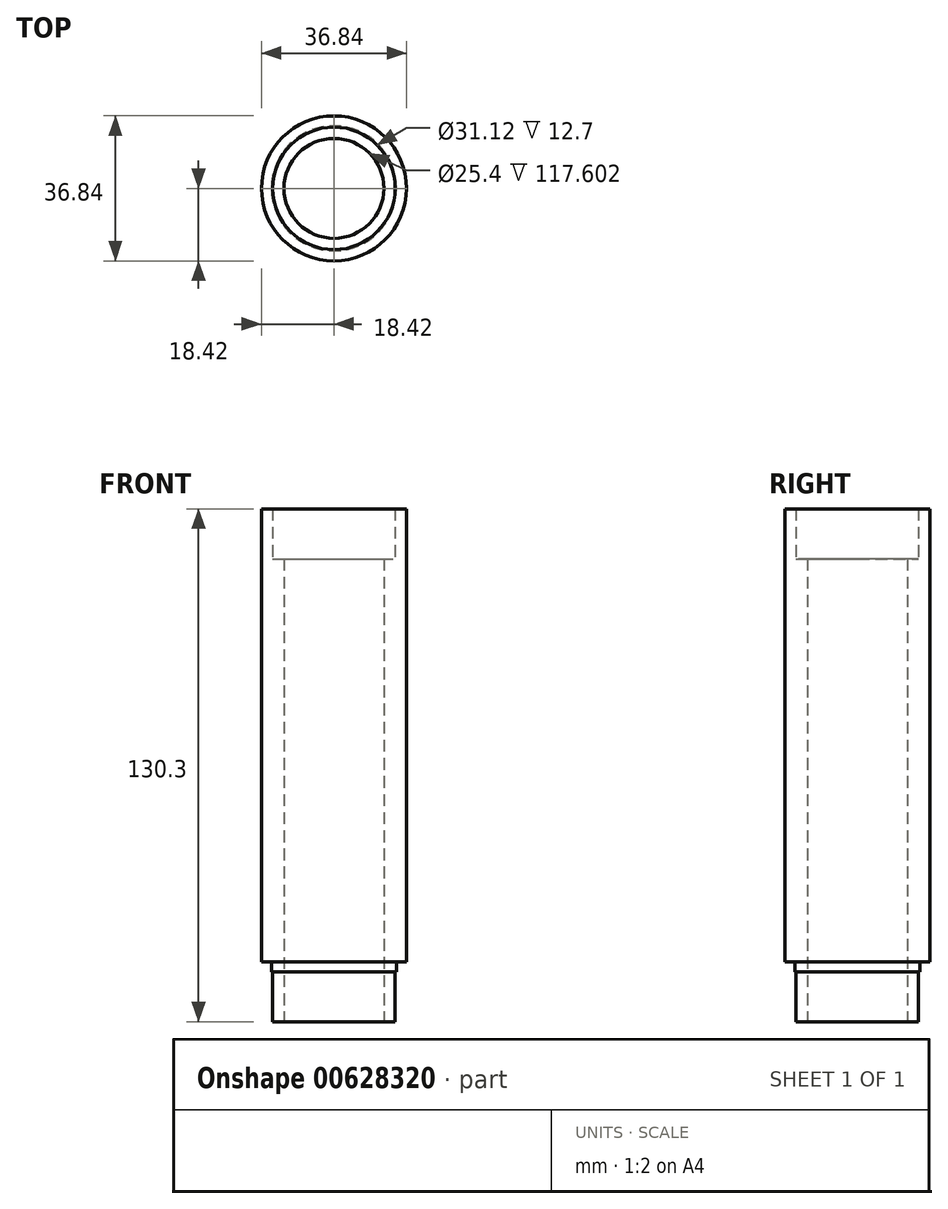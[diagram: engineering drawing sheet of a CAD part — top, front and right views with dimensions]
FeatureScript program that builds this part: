
annotation { "Feature Type Name" : "Feature", "Feature Type Description" : "" }
export const myFeature = defineFeature(function(context is Context, id is Id, definition is map)
    precondition{}
    {
        {
            var Q0;
            Q0=qCreatedBy(makeId("Front.planeOp"),FACE);
            var sketch = newSketch(context, id + "F0", { "sketchPlane" : qUnion([Q0])});
            skLineSegment(sketch, "E0.trimOffspring", {"start": v(18.41, 70.5) * mm, "end": v(18.42, -42.94) * mm});
            skLineSegment(sketch, "E1", {"start": v(18.42, -42.94) * mm, "end": v(15.87, -42.94) * mm});
            skLineSegment(sketch, "E2", {"start": v(15.87, -42.94) * mm, "end": v(15.87, -45.48) * mm});
            skLineSegment(sketch, "E3", {"start": v(12.7, 59.42) * mm, "end": v(12.7, -58.18) * mm});
            skLineSegment(sketch, "E4", {"start": v(12.7, -58.18) * mm, "end": v(15.56, -58.18) * mm});
            skLineSegment(sketch, "E5", {"start": v(15.56, -58.18) * mm, "end": v(15.56, -45.48) * mm});
            skLineSegment(sketch, "E6", {"start": v(15.56, -45.48) * mm, "end": v(15.87, -45.48) * mm});
            skLineSegment(sketch, "E7", {"start": v(15.56, 72.12) * mm, "end": v(15.56, 59.42) * mm});
            skLineSegment(sketch, "E8", {"start": v(15.56, 72.12) * mm, "end": v(18.41, 72.12) * mm});
            skLineSegment(sketch, "E9", {"start": v(18.41, 72.12) * mm, "end": v(18.41, 70.5) * mm});
            skLineSegment(sketch, "E10", {"start": v(15.56, 59.42) * mm, "end": v(12.7, 59.42) * mm});
            skLineSegment(sketch, "E11", {"start": v(0, 0) * mm, "end": v(0, 42.91) * mm});
            skSolve(sketch);
        }
        {
            var Q0;
            Q0=makeQuery(id+"F0.imprint","IMPRINT",FACE,{"disambiguationData":[TD([[makeQuery(id+"F0.imprint","IMPRINT",EDGE,{"derivedFrom":sQuery(id+"F0.wireOp",EDGE,"E0.trimOffspring")}),-1.0]])]});
            var Q1;
            Q1=sQuery(id+"F0.wireOp",EDGE,"E11");
            revolve(context, id + "F1", {"entities" : qUnion([Q0]), "axis" : qUnion([Q1]), "revolveType" : RevolveType.FULL});
        }
    });
